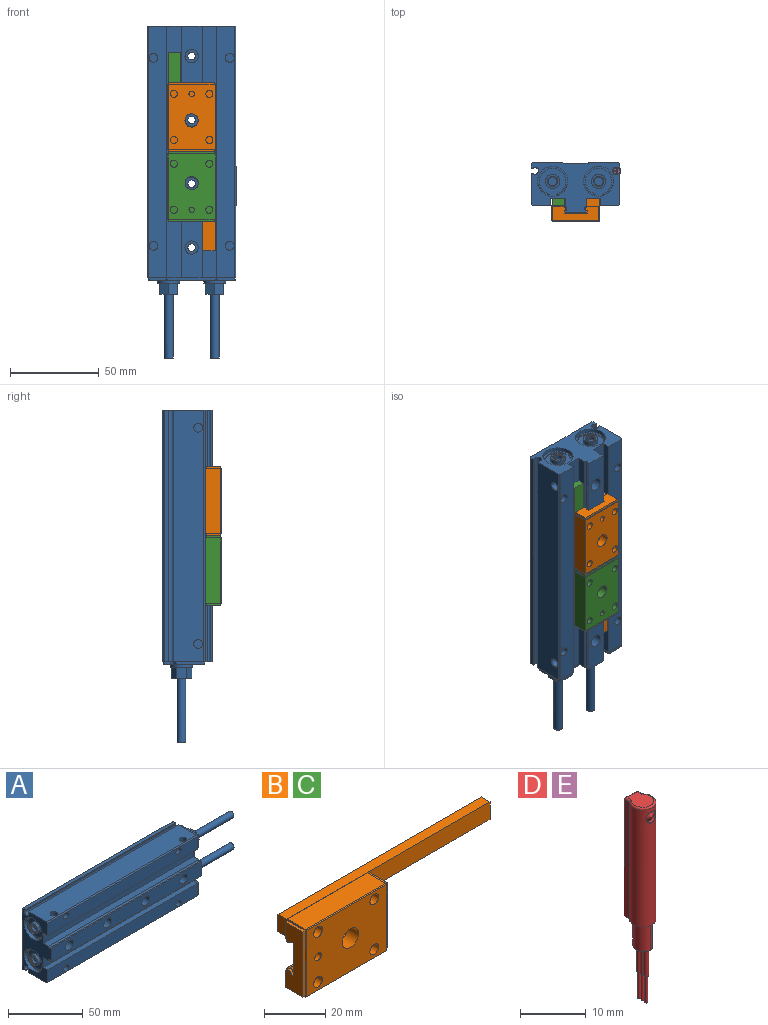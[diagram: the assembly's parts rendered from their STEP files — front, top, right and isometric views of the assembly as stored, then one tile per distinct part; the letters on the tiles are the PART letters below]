
ASSEMBLY  parts=5 mates=4
PART A: 186 faces, bbox 187.3x28x50 mm
  f0: cylinder r=2.5mm len=36mm, axis (-1,0,0), area 565.5mm2, adj f41,f172
  f1: cylinder r=2.5mm len=36mm, axis (-1,0,0), area 565.5mm2, adj f42,f164
  f2: cylinder r=6.28mm len=12.55mm, axis (-1,0,0), area 59.1mm2, adj f43,f157
  f3: cylinder r=6.28mm len=12.55mm, axis (-1,0,0), area 59.1mm2, adj f43,f150
  f4: cone r=2.5mm half-angle=45deg, axis (-1,0,0), area 9.6mm2, adj f8,f122
  f5: cone r=2.9mm half-angle=45deg, axis (-1,0,0), area 9.6mm2, adj f6,f124
  f6: cylinder r=2.5mm len=5mm, axis (1,0,0), area 31.4mm2, adj f5,f125
  f7: cylinder r=4mm len=8mm, axis (1,0,0), area 60.3mm2, adj f49,f124
  f8: cylinder r=2.5mm len=5mm, axis (1,0,0), area 31.4mm2, adj f4,f123
  f9: cylinder r=4mm len=8mm, axis (1,0,0), area 60.3mm2, adj f45,f122
  f10: cylinder r=3.75mm len=8mm, axis (0,-1,0), area 188.5mm2, adj f70,f121
  f11: cylinder r=3.75mm len=8mm, axis (0,-1,0), area 188.5mm2, adj f70,f120
  f12: cylinder r=3.75mm len=8mm, axis (0,-1,0), area 188.5mm2, adj f70,f119
  f13: cylinder r=3.75mm len=8mm, axis (0,-1,0), area 188.5mm2, adj f70,f118
  f14: cylinder r=2.5mm len=5.5mm, axis (0,-1,0), area 86.4mm2, adj f61,f117
  f15: cylinder r=2.5mm len=5.5mm, axis (0,-1,0), area 86.4mm2, adj f61,f116
  f16: cylinder r=2.5mm len=5.5mm, axis (0,-1,0), area 86.4mm2, adj f65,f115
  f17: cylinder r=2.5mm len=5.5mm, axis (0,-1,0), area 86.4mm2, adj f65,f114
  f18: cylinder r=2mm len=4mm, axis (0,1,0), area 37.7mm2, adj f57,f108
  f19: cylinder r=0.32mm len=0.65mm, axis (1,0,0), area 1mm2, adj f99,f106
  f20: cylinder r=0.32mm len=0.65mm, axis (1,0,0), area 1mm2, adj f99,f107
  f21: cylinder r=7.48mm len=14.96mm, axis (1,0,0), area 21.5mm2, adj f45,f99,f103,f104
  f22: cylinder r=0.32mm len=0.65mm, axis (1,0,0), area 1mm2, adj f90,f98
  f23: cylinder r=0.32mm len=0.65mm, axis (1,0,0), area 1mm2, adj f90,f97
  f24: cylinder r=7.48mm len=14.96mm, axis (1,0,0), area 21.5mm2, adj f49,f90,f93,f94
  f25: cylinder r=2.5mm len=5.5mm, axis (0,0,-1), area 86.4mm2, adj f52,f89
  f26: cylinder r=2.5mm len=5.5mm, axis (0,0,-1), area 86.4mm2, adj f52,f88
  f27: cylinder r=2.5mm len=5.5mm, axis (0,0,1), area 86.4mm2, adj f54,f87
  f28: cylinder r=2.5mm len=5.5mm, axis (0,0,1), area 86.4mm2, adj f54,f86
  f29: cylinder r=2.5mm len=11.7mm, axis (0,1,0), area 183.8mm2, adj f57,f85
  f30: cylinder r=2.5mm len=11.7mm, axis (0,1,0), area 183.8mm2, adj f57,f84
  f31: cylinder r=2.5mm len=11.7mm, axis (0,1,0), area 183.8mm2, adj f57,f83
  f32: cylinder r=2.5mm len=11.7mm, axis (0,1,0), area 183.8mm2, adj f57,f82
  f33: cylinder r=2mm len=142mm, axis (-1,0,0), area 1302.7mm2, adj f44,f53,f76,f77
  f34: cylinder r=1mm len=142mm, axis (1,0,0), area 446.1mm2, adj f44,f53,f71,f72
  f35: cylinder r=2.15mm len=8mm, axis (0,1,0), area 108.1mm2, adj f82,f119
  f36: cylinder r=2.15mm len=8mm, axis (0,1,0), area 108.1mm2, adj f83,f118
  f37: cylinder r=2.15mm len=8mm, axis (0,1,0), area 108.1mm2, adj f84,f120
  f38: cylinder r=2.15mm len=8mm, axis (0,1,0), area 108.1mm2, adj f85,f121
  f39: cylinder r=8.5mm len=17mm, axis (-1,0,0), area 132.1mm2, adj f48,f49,f50,f53,f90,f91,f92,f93
  f40: cylinder r=8.5mm len=17mm, axis (-1,0,0), area 132.1mm2, adj f45,f46,f47,f53,f99,f100,f101,f102
  f41: plane 11.55x10mm, normal (1,0,0), area 67mm2, adj f0,f158,f159,f160,f161,f162,f163
  f42: plane 11.55x10mm, normal (1,0,0), area 67mm2, adj f1,f151,f152,f153,f154,f155,f156
  f43: plane 49x23.4mm, normal (1,0,0), area 731.7mm2, adj f2,f3,f126,f127,f128,f129,f130,f131
  f44: plane 50x28mm, normal (1,0,0), area 167.2mm2, adj f33,f34,f51,f52,f54,f55,f56,f57
  f45: plane 15.98x14.96mm, normal (-1,0,0), area 129.8mm2, adj f9,f21,f40,f103,f104
  f46: plane 6.33x2.82mm, normal (-1,0,0), area 1.7mm2, adj f40,f101,f102
  f47: plane 6.33x2.82mm, normal (-1,0,0), area 1.7mm2, adj f40,f100,f105
  f48: plane 6.33x2.82mm, normal (-1,0,0), area 1.7mm2, adj f39,f91,f92
  f49: plane 15.98x14.96mm, normal (-1,0,0), area 129.8mm2, adj f7,f24,f39,f93,f94
  f50: plane 6.33x2.82mm, normal (-1,0,0), area 1.7mm2, adj f39,f95,f96
  f51: plane 142x2.35mm, normal (0,0,-1), area 333.7mm2, adj f44,f53,f76,f81
  f52: plane 142x17.15mm, normal (0,0,-1), area 2396mm2, adj f25,f26,f44,f53,f77,f80
  f53: plane 50x28mm, normal (-1,0,0), area 692.3mm2, adj f33,f34,f39,f40,f51,f52,f54,f55
  f54: plane 142x17.15mm, normal (0,0,1), area 2396mm2, adj f27,f28,f44,f53,f73,f79
  f55: plane 142x8.1mm, normal (0,-1,0), area 1150.2mm2, adj f44,f53,f64,f67
  f56: plane 142x0.3mm, normal (0,0.71,0.71), area 60.2mm2, adj f44,f53,f57,f66
  f57: plane 142x14mm, normal (0,1,0), area 1880.3mm2, adj f18,f29,f30,f31,f32,f44,f53,f56
  f58: plane 142x0.3mm, normal (0,0.71,-0.71), area 60.2mm2, adj f44,f53,f57,f59
  f59: plane 142x16.95mm, normal (0,1,0), area 2406.9mm2, adj f44,f53,f58,f78
  f60: plane 142x2.35mm, normal (0,0,1), area 333.7mm2, adj f44,f53,f74,f78
  f61: plane 142x10.25mm, normal (0,-1,0), area 1416.2mm2, adj f14,f15,f44,f53,f62,f79
  f62: plane 142x4mm, normal (0,0,-1), area 568mm2, adj f44,f53,f61,f63
  f63: plane 142x8.1mm, normal (0,-1,0), area 1150.2mm2, adj f44,f53,f62,f72
  f64: plane 142x4mm, normal (0,0,1), area 568mm2, adj f44,f53,f55,f65
  f65: plane 142x10.25mm, normal (0,-1,0), area 1416.2mm2, adj f16,f17,f44,f53,f64,f80
  f66: plane 142x16.95mm, normal (0,1,0), area 2406.9mm2, adj f44,f53,f56,f81
  f67: plane 142x5mm, normal (0,0,-1), area 710mm2, adj f44,f53,f55,f68
  f68: cylinder r=1mm len=142mm, axis (1,0,0), area 446.1mm2, adj f44,f53,f67,f69
  f69: plane 142x1mm, normal (0,0,-1), area 142mm2, adj f44,f53,f68,f70
  f70: plane 142x11.8mm, normal (0,-1,0), area 1498.9mm2, adj f10,f11,f12,f13,f44,f53,f69,f71
  f71: plane 142x1mm, normal (0,0,1), area 142mm2, adj f34,f44,f53,f70
  f72: plane 142x5mm, normal (0,0,1), area 710mm2, adj f34,f44,f53,f63
  f73: plane 142x0.88mm, normal (0,1,0), area 124.6mm2, adj f44,f53,f54,f75
  f74: plane 142x0.88mm, normal (0,-1,0), area 124.6mm2, adj f44,f53,f60,f75
  f75: cylinder r=2mm len=142mm, axis (-1,0,0), area 1302.7mm2, adj f44,f53,f73,f74
  f76: plane 142x0.88mm, normal (0,-1,0), area 124.6mm2, adj f33,f44,f51,f53
  f77: plane 142x0.88mm, normal (0,1,0), area 124.6mm2, adj f33,f44,f52,f53
  f78: plane 142x0.75mm, normal (0,0.71,0.71), area 150.6mm2, adj f44,f53,f59,f60
  f79: plane 142x0.75mm, normal (0,-0.71,0.71), area 150.6mm2, adj f44,f53,f54,f61
  f80: plane 142x0.75mm, normal (0,-0.71,-0.71), area 150.6mm2, adj f44,f52,f53,f65
  f81: plane 142x0.75mm, normal (0,0.71,-0.71), area 150.6mm2, adj f44,f51,f53,f66
  f82: plane 5x5mm, normal (0,1,0), area 5.1mm2, adj f32,f35
  f83: plane 5x5mm, normal (0,1,0), area 5.1mm2, adj f31,f36
  f84: plane 5x5mm, normal (0,1,0), area 5.1mm2, adj f30,f37
  f85: plane 5x5mm, normal (0,1,0), area 5.1mm2, adj f29,f38
  f86: plane 5x5mm, normal (0,0,1), area 19.6mm2, adj f28
  f87: plane 5x5mm, normal (0,0,1), area 19.6mm2, adj f27
  f88: plane 5x5mm, normal (0,0,-1), area 19.6mm2, adj f26
  f89: plane 5x5mm, normal (0,0,-1), area 19.6mm2, adj f25
  f90: plane 16.99x16.71mm, normal (-1,0,0), area 42.9mm2, adj f22,f23,f24,f39,f91,f92,f93,f94
  f91: cylinder r=8.5mm len=6mm, axis (1,0,0), area 3.4mm2, adj f39,f48,f90,f92
  f92: plane 0.5x0.33mm, normal (0,0.71,-0.71), area 0.2mm2, adj f39,f48,f90,f91
  f93: plane 0.99x0.5mm, normal (0,-0.26,0.97), area 0.5mm2, adj f24,f39,f49,f90
  f94: plane 0.99x0.5mm, normal (0,-0.26,-0.97), area 0.5mm2, adj f24,f39,f49,f90
  f95: plane 0.5x0.33mm, normal (0,0.71,0.71), area 0.2mm2, adj f39,f50,f90,f96
  f96: cylinder r=8.5mm len=6mm, axis (1,0,0), area 3.4mm2, adj f39,f50,f90,f95
  f97: plane 0.65x0.65mm, normal (-1,0,0), area 0.3mm2, adj f23
  f98: plane 0.65x0.65mm, normal (-1,0,0), area 0.3mm2, adj f22
  f99: plane 16.99x16.71mm, normal (-1,0,0), area 42.9mm2, adj f19,f20,f21,f40,f100,f101,f102,f103
  f100: cylinder r=8.5mm len=6mm, axis (1,0,0), area 3.4mm2, adj f40,f47,f99,f105
  f101: cylinder r=8.5mm len=6mm, axis (1,0,0), area 3.4mm2, adj f40,f46,f99,f102
  f102: plane 0.5x0.33mm, normal (0,0.71,-0.71), area 0.2mm2, adj f40,f46,f99,f101
  f103: plane 0.99x0.5mm, normal (0,-0.26,0.97), area 0.5mm2, adj f21,f40,f45,f99
  f104: plane 0.99x0.5mm, normal (0,-0.26,-0.97), area 0.5mm2, adj f21,f40,f45,f99
  f105: plane 0.5x0.33mm, normal (0,0.71,0.71), area 0.2mm2, adj f40,f47,f99,f100
  f106: plane 0.65x0.65mm, normal (-1,0,0), area 0.3mm2, adj f19
  f107: plane 0.65x0.65mm, normal (-1,0,0), area 0.3mm2, adj f20
  f108: plane 4x4mm, normal (0,1,0), area 12.6mm2, adj f18
  f109: cylinder r=2mm len=4mm, axis (0,1,0), area 18.8mm2, adj f57,f110,f112,f113
  f110: plane 3x1mm, normal (0,0,1), area 3mm2, adj f57,f109,f111,f113
  f111: cylinder r=2mm len=4mm, axis (0,1,0), area 18.8mm2, adj f57,f110,f112,f113
  f112: plane 3x1mm, normal (0,0,-1), area 3mm2, adj f57,f109,f111,f113
  f113: plane 5x4mm, normal (0,1,0), area 16.6mm2, adj f109,f110,f111,f112
  f114: plane 5x5mm, normal (0,-1,0), area 19.6mm2, adj f17
  f115: plane 5x5mm, normal (0,-1,0), area 19.6mm2, adj f16
  f116: plane 5x5mm, normal (0,-1,0), area 19.6mm2, adj f15
  f117: plane 5x5mm, normal (0,-1,0), area 19.6mm2, adj f14
  f118: plane 7.5x7.5mm, normal (0,-1,0), area 29.7mm2, adj f13,f36
  f119: plane 7.5x7.5mm, normal (0,-1,0), area 29.7mm2, adj f12,f35
  f120: plane 7.5x7.5mm, normal (0,-1,0), area 29.7mm2, adj f11,f37
  f121: plane 7.5x7.5mm, normal (0,-1,0), area 29.7mm2, adj f10,f38
  f122: plane 8x8mm, normal (-1,0,0), area 23.8mm2, adj f4,f9
  f123: plane 5x5mm, normal (-1,0,0), area 19.6mm2, adj f8
  f124: plane 8x8mm, normal (-1,0,0), area 23.8mm2, adj f5,f7
  f125: plane 5x5mm, normal (-1,0,0), area 19.6mm2, adj f6
  f126: cylinder r=2.5mm len=2.5mm, axis (-1,0,0), area 5.9mm2, adj f43,f44,f127,f149
  f127: plane 1.5x1.2mm, normal (0,1,0), area 1.8mm2, adj f43,f44,f126,f128
  f128: cylinder r=0.5mm len=1.5mm, axis (-1,0,0), area 1.2mm2, adj f43,f44,f127,f129
  f129: plane 15.7x1.5mm, normal (0,0,1), area 23.6mm2, adj f43,f44,f128,f130
  f130: cylinder r=0.5mm len=1.5mm, axis (-1,0,0), area 1.2mm2, adj f43,f44,f129,f131
  f131: plane 9.3x1.5mm, normal (0,-1,0), area 14mm2, adj f43,f44,f130,f132
  f132: cylinder r=0.5mm len=1.5mm, axis (-1,0,0), area 1.2mm2, adj f43,f44,f131,f133
  f133: plane 3x1.5mm, normal (0,0,-1), area 4.5mm2, adj f43,f44,f132,f134
  f134: cylinder r=0.5mm len=1.5mm, axis (-1,0,0), area 1.2mm2, adj f43,f44,f133,f135
  f135: plane 27.4x1.5mm, normal (0,-1,0), area 41.1mm2, adj f43,f44,f134,f136
  f136: cylinder r=0.5mm len=1.5mm, axis (-1,0,0), area 1.2mm2, adj f43,f44,f135,f137
  f137: plane 3x1.5mm, normal (0,0,1), area 4.5mm2, adj f43,f44,f136,f138
  f138: cylinder r=0.5mm len=1.5mm, axis (-1,0,0), area 1.2mm2, adj f43,f44,f137,f139
  f139: plane 9.3x1.5mm, normal (0,-1,0), area 14mm2, adj f43,f44,f138,f140
  f140: cylinder r=0.5mm len=1.5mm, axis (-1,0,0), area 1.2mm2, adj f43,f44,f139,f141
  f141: plane 15.7x1.5mm, normal (0,0,-1), area 23.6mm2, adj f43,f44,f140,f142
  f142: cylinder r=0.5mm len=1.5mm, axis (-1,0,0), area 1.2mm2, adj f43,f44,f141,f143
  f143: plane 1.5x1.2mm, normal (0,1,0), area 1.8mm2, adj f43,f44,f142,f144
  f144: cylinder r=2.5mm len=2.5mm, axis (-1,0,0), area 5.9mm2, adj f43,f44,f143,f145
  f145: plane 3.7x1.5mm, normal (0,0,-1), area 5.6mm2, adj f43,f44,f144,f146
  f146: cylinder r=0.5mm len=1.5mm, axis (-1,0,0), area 1.2mm2, adj f43,f44,f145,f147
  f147: plane 39.6x1.5mm, normal (0,1,0), area 59.4mm2, adj f43,f44,f146,f148
  f148: cylinder r=0.5mm len=1.5mm, axis (-1,0,0), area 1.2mm2, adj f43,f44,f147,f149
  f149: plane 3.7x1.5mm, normal (0,0,1), area 5.6mm2, adj f43,f44,f126,f148
  f150: plane 12.55x12.55mm, normal (1,0,0), area 37.1mm2, adj f3,f151,f152,f153,f154,f155,f156
  f151: plane 6.3x5.77mm, normal (0,0,-1), area 36.4mm2, adj f42,f150,f152,f156
  f152: plane 6.3x5mm, normal (0,-0.87,-0.5), area 36.4mm2, adj f42,f150,f151,f153
  f153: plane 6.3x5mm, normal (0,-0.87,0.5), area 36.4mm2, adj f42,f150,f152,f154
  f154: plane 6.3x5.77mm, normal (0,0,1), area 36.4mm2, adj f42,f150,f153,f155
  f155: plane 6.3x5mm, normal (0,0.87,0.5), area 36.4mm2, adj f42,f150,f154,f156
  f156: plane 6.3x5mm, normal (0,0.87,-0.5), area 36.4mm2, adj f42,f150,f151,f155
  f157: plane 12.55x12.55mm, normal (1,0,0), area 37.1mm2, adj f2,f158,f159,f160,f161,f162,f163
  f158: plane 6.3x5mm, normal (0,0.87,0.5), area 36.4mm2, adj f41,f157,f159,f163
  f159: plane 6.3x5mm, normal (0,0.87,-0.5), area 36.4mm2, adj f41,f157,f158,f160
  f160: plane 6.3x5.77mm, normal (0,0,-1), area 36.4mm2, adj f41,f157,f159,f161
  f161: plane 6.3x5mm, normal (0,-0.87,-0.5), area 36.4mm2, adj f41,f157,f160,f162
  f162: plane 6.3x5mm, normal (0,-0.87,0.5), area 36.4mm2, adj f41,f157,f161,f163
  f163: plane 6.3x5.77mm, normal (0,0,1), area 36.4mm2, adj f41,f157,f158,f162
  f164: plane 5x5mm, normal (1,0,0), area 11.8mm2, adj f1,f165,f166,f167,f168,f169,f170
  f165: plane 3x1.69mm, normal (0,-0.98,-0.22), area 5.2mm2, adj f164,f166,f170,f171
  f166: plane 3x1.27mm, normal (0,-0.68,0.74), area 5.2mm2, adj f164,f165,f167,f171
  f167: plane 3x1.65mm, normal (0,0.3,0.95), area 5.2mm2, adj f164,f166,f168,f171
  f168: plane 3x1.69mm, normal (0,0.98,0.22), area 5.2mm2, adj f164,f167,f169,f171
  f169: plane 3x1.27mm, normal (0,0.68,-0.74), area 5.2mm2, adj f164,f168,f170,f171
  f170: plane 3x1.65mm, normal (0,-0.3,-0.95), area 5.2mm2, adj f164,f165,f169,f171
  f171: plane 3.38x3.31mm, normal (1,0,0), area 7.8mm2, adj f165,f166,f167,f168,f169,f170
  f172: plane 5x5mm, normal (1,0,0), area 11.8mm2, adj f0,f173,f174,f175,f176,f177,f178
  f173: plane 3x1.63mm, normal (0,-0.33,0.94), area 5.2mm2, adj f172,f174,f178,f179
  f174: plane 3x1.31mm, normal (0,0.65,0.76), area 5.2mm2, adj f172,f173,f175,f179
  f175: plane 3x1.7mm, normal (0,0.98,-0.19), area 5.2mm2, adj f172,f174,f176,f179
  f176: plane 3x1.63mm, normal (0,0.33,-0.94), area 5.2mm2, adj f172,f175,f177,f179
  f177: plane 3x1.31mm, normal (0,-0.65,-0.76), area 5.2mm2, adj f172,f176,f178,f179
  f178: plane 3x1.7mm, normal (0,-0.98,0.19), area 5.2mm2, adj f172,f173,f177,f179
  f179: plane 3.4x3.27mm, normal (1,0,0), area 7.8mm2, adj f173,f174,f175,f176,f177,f178
  f180: cylinder r=8.5mm len=17mm, axis (1,0,0), area 149.5mm2, adj f181,f182
  f181: plane 17x17mm, normal (1,0,0), area 227mm2, adj f180
  f182: plane 17x17mm, normal (-1,0,0), area 227mm2, adj f180
  f183: cylinder r=8.5mm len=17mm, axis (1,0,0), area 149.5mm2, adj f184,f185
  f184: plane 17x17mm, normal (1,0,0), area 227mm2, adj f183
  f185: plane 17x17mm, normal (-1,0,0), area 227mm2, adj f183
PART B: 67 faces, bbox 95.2x13x27 mm
  f0: cylinder r=2mm len=4mm, axis (0,-1,0), area 50.3mm2, adj f14,f61
  f1: cylinder r=2mm len=4mm, axis (0,-1,0), area 50.3mm2, adj f14,f60
  f2: cylinder r=2mm len=4mm, axis (0,-1,0), area 50.3mm2, adj f14,f59
  f3: cylinder r=2mm len=4mm, axis (0,-1,0), area 50.3mm2, adj f14,f58
  f4: cylinder r=1.5mm len=3mm, axis (0,-1,0), area 28.3mm2, adj f14,f57
  f5: cylinder r=3.75mm len=7.5mm, axis (0,-1,0), area 117.8mm2, adj f14,f19
  f6: cylinder r=1mm len=2mm, axis (1,0,0), area 3.8mm2, adj f9,f10,f37,f42,f43,f50
  f7: cylinder r=1mm len=2mm, axis (-1,0,0), area 3.8mm2, adj f11,f12,f23,f27,f28,f35
  f8: cylinder r=1mm len=37mm, axis (1,0,0), area 116.2mm2, adj f9,f10,f11,f12,f20,f21,f23,f38
  f9: plane 13x1.53mm, normal (-1,0,0), area 7.5mm2, adj f6,f8,f17,f18,f19,f20,f43,f44
  f10: plane 27x13mm, normal (-1,0,0), area 57.3mm2, adj f6,f8,f13,f14,f15,f16,f17,f21
  f11: plane 13x1.53mm, normal (1,0,0), area 7.5mm2, adj f7,f8,f17,f18,f19,f20,f28,f29
  f12: plane 27x9mm, normal (1,0,0), area 29.3mm2, adj f7,f8,f13,f14,f15,f16,f17,f21
  f13: plane 37x8.5mm, normal (0,0,-1), area 314.5mm2, adj f10,f12,f55,f56
  f14: plane 37x26.5mm, normal (0,-1,0), area 879mm2, adj f0,f1,f2,f3,f4,f5,f10,f12
  f15: plane 37x8.5mm, normal (0,0,1), area 314.5mm2, adj f10,f12,f51,f52
  f16: plane 37x0.75mm, normal (0,0,-1), area 27.7mm2, adj f10,f12,f17,f53
  f17: cylinder r=1mm len=37mm, axis (1,0,0), area 116.2mm2, adj f9,f10,f11,f12,f16,f18,f36,f37
  f18: plane 37x1mm, normal (0,0,-1), area 37mm2, adj f9,f11,f17,f19
  f19: plane 37x12mm, normal (0,1,0), area 399.8mm2, adj f5,f9,f11,f18,f20
  f20: plane 37x1mm, normal (0,0,1), area 37mm2, adj f8,f9,f11,f19
  f21: plane 37x0.75mm, normal (0,0,1), area 27.7mm2, adj f8,f10,f12,f54
  f22: plane 37x7mm, normal (0,1,0), area 259mm2, adj f10,f12,f54,f55
  f23: plane 1.94x1.5mm, normal (-1,0,0), area 2.2mm2, adj f7,f8
  f24: plane 26x1.2mm, normal (0,-1,0), area 31.2mm2, adj f12,f25,f34,f35
  f25: plane 8x1.2mm, normal (0,0,-1), area 9.6mm2, adj f12,f24,f26,f35
  f26: plane 6.5x1.2mm, normal (0,1,0), area 7.8mm2, adj f12,f25,f27,f35
  f27: plane 1.2x0.5mm, normal (0,0,1), area 0.6mm2, adj f7,f12,f26,f35
  f28: plane 1.5x1.2mm, normal (0,0,1), area 1.8mm2, adj f7,f11,f29,f35
  f29: plane 13x1.2mm, normal (0,1,0), area 15.6mm2, adj f11,f28,f30,f35
  f30: plane 1.5x1.2mm, normal (0,0,-1), area 1.8mm2, adj f11,f29,f31,f35
  f31: cylinder r=1mm len=2mm, axis (-1,0,0), area 3.8mm2, adj f11,f12,f30,f32,f35,f36
  f32: plane 1.2x0.5mm, normal (0,0,-1), area 0.6mm2, adj f12,f31,f33,f35
  f33: plane 6.5x1.2mm, normal (0,1,0), area 7.8mm2, adj f12,f32,f34,f35
  f34: plane 8x1.2mm, normal (0,0,1), area 9.6mm2, adj f12,f24,f33,f35
  f35: plane 26x8mm, normal (1,0,0), area 159.1mm2, adj f7,f24,f25,f26,f27,f28,f29,f30
  f36: plane 1.94x1.5mm, normal (-1,0,0), area 2.2mm2, adj f17,f31
  f37: plane 1.94x1.5mm, normal (1,0,0), area 2.2mm2, adj f6,f17
  f38: plane 1.94x1.5mm, normal (1,0,0), area 2.2mm2, adj f8,f46
  f39: plane 26x1.2mm, normal (0,-1,0), area 31.2mm2, adj f10,f40,f49,f50
  f40: plane 8x1.2mm, normal (0,0,1), area 9.6mm2, adj f10,f39,f41,f50
  f41: plane 6.5x1.2mm, normal (0,1,0), area 7.8mm2, adj f10,f40,f42,f50
  f42: plane 1.2x0.5mm, normal (0,0,-1), area 0.6mm2, adj f6,f10,f41,f50
  f43: plane 1.5x1.2mm, normal (0,0,-1), area 1.8mm2, adj f6,f9,f44,f50
  f44: plane 13x1.2mm, normal (0,1,0), area 15.6mm2, adj f9,f43,f45,f50
  f45: plane 1.5x1.2mm, normal (0,0,1), area 1.8mm2, adj f9,f44,f46,f50
  f46: cylinder r=1mm len=2mm, axis (1,0,0), area 3.8mm2, adj f9,f10,f38,f45,f47,f50
  f47: plane 1.2x0.5mm, normal (0,0,1), area 0.6mm2, adj f10,f46,f48,f50
  f48: plane 6.5x1.2mm, normal (0,1,0), area 7.8mm2, adj f10,f47,f49,f50
  f49: plane 8x1.2mm, normal (0,0,-1), area 9.6mm2, adj f10,f39,f48,f50
  f50: plane 26x8mm, normal (-1,0,0), area 159.1mm2, adj f6,f39,f40,f41,f42,f43,f44,f45
  f51: plane 37x0.25mm, normal (0,0.71,0.71), area 13.1mm2, adj f10,f12,f15,f63
  f52: plane 37x0.25mm, normal (0,-0.71,0.71), area 13.1mm2, adj f10,f12,f14,f15
  f53: plane 37x0.25mm, normal (0,0.71,-0.71), area 13.1mm2, adj f10,f12,f16,f65
  f54: plane 37x0.25mm, normal (0,0.71,0.71), area 13.1mm2, adj f10,f12,f21,f22
  f55: plane 37x0.25mm, normal (0,0.71,-0.71), area 13.1mm2, adj f10,f12,f13,f22
  f56: plane 37x0.25mm, normal (0,-0.71,-0.71), area 13.1mm2, adj f10,f12,f13,f14
  f57: plane 3x3mm, normal (0,-1,0), area 7.1mm2, adj f4
  f58: plane 4x4mm, normal (0,-1,0), area 12.6mm2, adj f3
  f59: plane 4x4mm, normal (0,-1,0), area 12.6mm2, adj f2
  f60: plane 4x4mm, normal (0,-1,0), area 12.6mm2, adj f1
  f61: plane 4x4mm, normal (0,-1,0), area 12.6mm2, adj f0
  f62: plane 57x7mm, normal (0,-1,0), area 399mm2, adj f12,f63,f64,f65
  f63: plane 94x4mm, normal (0,0,1), area 376mm2, adj f10,f51,f62,f64,f66
  f64: plane 7x4mm, normal (1,0,0), area 28mm2, adj f62,f63,f65,f66
  f65: plane 94x4mm, normal (0,0,-1), area 376mm2, adj f10,f53,f62,f64,f66
  f66: plane 94x7mm, normal (0,1,0), area 658mm2, adj f10,f63,f64,f65
PART C: same geometry as B
PART D: 38 faces, bbox 5.8x5.2x37.4 mm
  f0: cone r=1732.05mm half-angle=60deg, axis (0,1,0), area 3.8mm2, adj f2
  f1: torus R=1.7mm, axis (0,0,1), area 4.3mm2, adj f10,f19,f31,f32
  f2: cylinder r=1.03mm len=2.05mm, axis (0,1,0), area 3.8mm2, adj f0,f10
  f3: cylinder r=0.25mm len=5mm, axis (0,0,1), area 7.9mm2, adj f13,f30
  f4: cylinder r=0.38mm len=5mm, axis (0,0,1), area 11.8mm2, adj f13,f14
  f5: cylinder r=0.25mm len=5mm, axis (0,0,1), area 7.9mm2, adj f15,f29
  f6: cylinder r=0.25mm len=5mm, axis (0,0,1), area 7.9mm2, adj f16,f28
  f7: cylinder r=0.38mm len=5mm, axis (0,0,1), area 11.8mm2, adj f14,f16
  f8: cylinder r=0.38mm len=5mm, axis (0,0,1), area 11.8mm2, adj f14,f15
  f9: bspline ~5.5x3.2mm, area 23.2mm2, adj f14,f17,f27
  f10: cylinder r=2mm len=21.7mm, axis (0,0,1), area 202.1mm2, adj f1,f2,f17,f20,f21
  f11: cylinder r=1.03mm len=2.05mm, axis (0,1,0), area 5mm2, adj f12,f18,f34,f35,f36,f37
  f12: plane 1.55x1.55mm, normal (0,1,0), area 1.1mm2, adj f11,f36
  f13: plane 0.75x0.75mm, normal (0,0,-1), area 0.2mm2, adj f3,f4
  f14: plane 3.61x3.11mm, normal (0,0,-1), area 5.5mm2, adj f4,f7,f8,f9,f27
  f15: plane 0.75x0.75mm, normal (0,0,-1), area 0.2mm2, adj f5,f8
  f16: plane 0.75x0.75mm, normal (0,0,-1), area 0.2mm2, adj f6,f7
  f17: plane 5.01x4.41mm, normal (0,0,-1), area 8mm2, adj f9,f10,f18,f20,f21,f27
  f18: plane 21.7x2.8mm, normal (0,1,0), area 52.5mm2, adj f11,f17,f20,f21,f22,f23,f24,f25
  f19: plane 4x3.4mm, normal (0,0,1), area 10.7mm2, adj f1,f31,f32,f33
  f20: plane 21.7x1.17mm, normal (-1,0,0), area 25.4mm2, adj f10,f17,f18,f31
  f21: plane 21.7x1.17mm, normal (1,0,0), area 25.4mm2, adj f10,f17,f18,f32
  f22: plane 2.5x0.01mm, normal (1,0,0), area 0mm2, adj f18,f23,f25,f26
  f23: plane 2x0.01mm, normal (0,0,-1), area 0mm2, adj f18,f22,f24,f26
  f24: plane 2.5x0.01mm, normal (-1,0,0), area 0mm2, adj f18,f23,f25,f26
  f25: plane 2x0.01mm, normal (0,0,1), area 0mm2, adj f18,f22,f24,f26
  f26: plane 2.5x2mm, normal (0,1,0), area 5mm2, adj f22,f23,f24,f25
  f27: bspline ~5.5x3.2mm, area 23.2mm2, adj f9,f14,f17
  f28: plane 0.5x0.5mm, normal (0,0,-1), area 0.2mm2, adj f6
  f29: plane 0.5x0.5mm, normal (0,0,-1), area 0.2mm2, adj f5
  f30: plane 0.5x0.5mm, normal (0,0,-1), area 0.2mm2, adj f3
  f31: cylinder r=0.3mm len=1.3mm, axis (0,1,0), area 0.5mm2, adj f1,f19,f20,f33
  f32: cylinder r=0.3mm len=1.3mm, axis (0,1,0), area 0.5mm2, adj f1,f19,f21,f33
  f33: cylinder r=0.3mm len=2.8mm, axis (1,0,0), area 1.2mm2, adj f18,f19,f31,f32
  f34: plane 1.55x1.55mm, normal (0,1,0), area 1.1mm2, adj f11,f35
  f35: plane 1.41x1.41mm, normal (0.71,0,-0.71), area 1mm2, adj f11,f34,f37
  f36: plane 1.41x1.41mm, normal (-0.71,0,0.71), area 1mm2, adj f11,f12,f37
  f37: plane 1.76x1.76mm, normal (0,1,0), area 1mm2, adj f11,f35,f36
PART E: same geometry as D
PLACE A rot(axis=(0,1,0),90deg) t=(-0.22,-7.48,22.69)mm fixed
PLACE B rot(axis=(0,1,0),90deg) t=(-0.22,-7.48,42.39)mm
PLACE C rot(axis=(0,-1,0),90deg) t=(-0.22,-7.48,2.99)mm
PLACE D rot(axis=(0,0,-1),90deg) t=(22.58,11.92,14.69)mm
PLACE E rot(axis=(0.71,0.71,0),180deg) t=(21.98,11.92,30.69)mm
MATE fastened D.f1 <-> A.f75  axis (0,0,-1) through (22.58,11.92,-7.31)mm
MATE fastened E.f17 <-> A.f75  axis (0,0,1) through (22.58,11.92,52.69)mm
MATE slider A.f53 <-> B.f50  axis (0,0,1) through (-0.22,-11.48,93.69)mm
MATE slider A.f44 <-> C.f50  axis (0,0,-1) through (-0.22,-11.48,-48.31)mm
